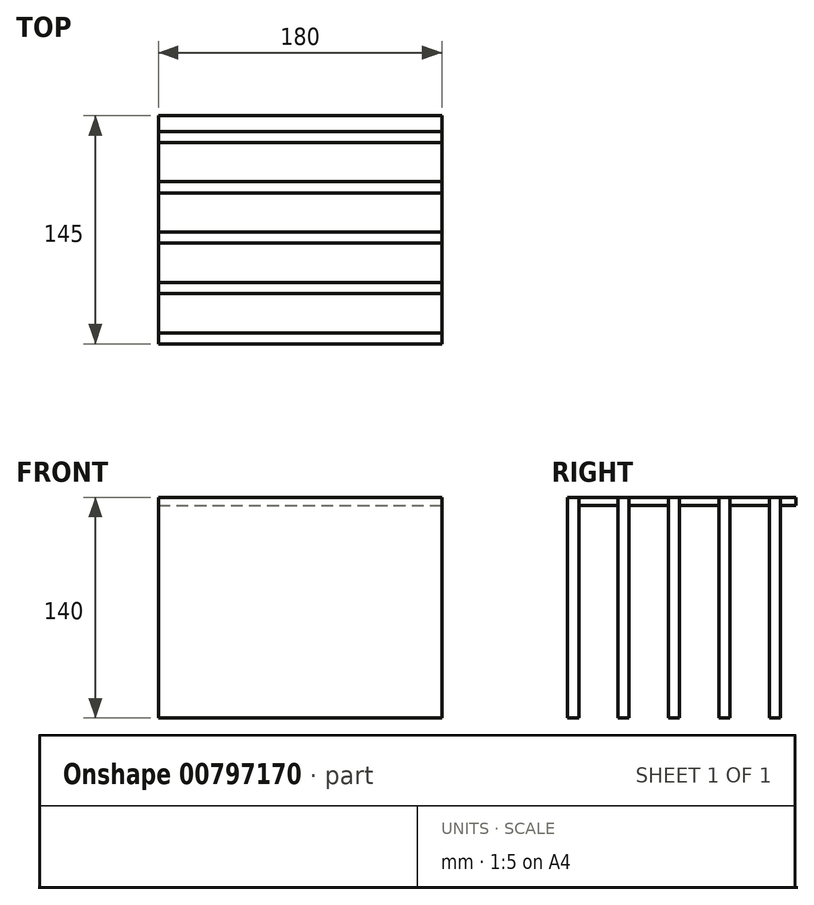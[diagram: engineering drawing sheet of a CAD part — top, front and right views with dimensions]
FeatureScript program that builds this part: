
annotation { "Feature Type Name" : "Feature", "Feature Type Description" : "" }
export const myFeature = defineFeature(function(context is Context, id is Id, definition is map)
    precondition{}
    {
        {
            var Q0;
            Q0=qCreatedBy(makeId("Top.planeOp"),FACE);
            var sketch = newSketch(context, id + "F0", { "sketchPlane" : qUnion([Q0])});
            skLineSegment(sketch, "E0.bottom", {"start": v(-72.5, 73) * mm, "end": v(107.5, 73) * mm});
            skLineSegment(sketch, "E0.top", {"start": v(-72.5, -72) * mm, "end": v(107.5, -72) * mm});
            skLineSegment(sketch, "E0.left", {"start": v(-72.5, 73) * mm, "end": v(-72.5, -72) * mm});
            skLineSegment(sketch, "E0.right", {"start": v(107.5, 73) * mm, "end": v(107.5, -72) * mm});
            skLineSegment(sketch, "E1.top", {"start": v(-72.5, -65) * mm, "end": v(107.5, -65) * mm});
            skLineSegment(sketch, "E1.left", {"start": v(-72.5, -72) * mm, "end": v(-72.5, -65) * mm});
            skLineSegment(sketch, "E1.right", {"start": v(107.5, -72) * mm, "end": v(107.5, -65) * mm});
            skLineSegment(sketch, "E2.bottom", {"start": v(-72.5, -40) * mm, "end": v(107.5, -40) * mm});
            skLineSegment(sketch, "E2.top", {"start": v(-72.5, -33) * mm, "end": v(107.5, -33) * mm});
            skLineSegment(sketch, "E2.left", {"start": v(-72.5, -40) * mm, "end": v(-72.5, -33) * mm});
            skLineSegment(sketch, "E2.right", {"start": v(107.5, -40) * mm, "end": v(107.5, -33) * mm});
            skLineSegment(sketch, "E3.bottom", {"start": v(-72.5, -8) * mm, "end": v(107.5, -8) * mm});
            skLineSegment(sketch, "E3.top", {"start": v(-72.5, -1) * mm, "end": v(107.5, -1) * mm});
            skLineSegment(sketch, "E3.left", {"start": v(-72.5, -8) * mm, "end": v(-72.5, -1) * mm});
            skLineSegment(sketch, "E3.right", {"start": v(107.5, -8) * mm, "end": v(107.5, -1) * mm});
            skLineSegment(sketch, "E4.bottom", {"start": v(-72.5, 24) * mm, "end": v(107.5, 24) * mm});
            skLineSegment(sketch, "E4.top", {"start": v(-72.5, 31) * mm, "end": v(107.5, 31) * mm});
            skLineSegment(sketch, "E4.left", {"start": v(-72.5, 24) * mm, "end": v(-72.5, 31) * mm});
            skLineSegment(sketch, "E4.right", {"start": v(107.5, 24) * mm, "end": v(107.5, 31) * mm});
            skLineSegment(sketch, "E5.bottom", {"start": v(-72.5, 56) * mm, "end": v(107.5, 56) * mm});
            skLineSegment(sketch, "E5.top", {"start": v(-72.5, 63) * mm, "end": v(107.5, 63) * mm});
            skLineSegment(sketch, "E5.left", {"start": v(-72.5, 56) * mm, "end": v(-72.5, 63) * mm});
            skLineSegment(sketch, "E5.right", {"start": v(107.5, 56) * mm, "end": v(107.5, 63) * mm});
            skSolve(sketch);
        }
        {
            var Q0;
            {var subQ0=sQuery(id+"F0.wireOp",EDGE,"E4.top");Q0=makeQuery(id+"F0.imprint","IMPRINT",FACE,{"disambiguationData":[TD([[makeQuery(id+"F0.imprint","IMPRINT",EDGE,{"derivedFrom":subQ0}),1.0]])]});}
            var Q1;
            {var subQ0=sQuery(id+"F0.wireOp",EDGE,"E0.bottom");Q1=makeQuery(id+"F0.imprint","IMPRINT",FACE,{"disambiguationData":[TD([[makeQuery(id+"F0.imprint","IMPRINT",EDGE,{"derivedFrom":subQ0}),-1.0]])]});}
            var Q2;
            {var subQ0=sQuery(id+"F0.wireOp",EDGE,"E3.top");Q2=makeQuery(id+"F0.imprint","IMPRINT",FACE,{"disambiguationData":[TD([[makeQuery(id+"F0.imprint","IMPRINT",EDGE,{"derivedFrom":subQ0}),1.0]])]});}
            var Q3;
            {var subQ0=sQuery(id+"F0.wireOp",EDGE,"E2.top");Q3=makeQuery(id+"F0.imprint","IMPRINT",FACE,{"disambiguationData":[TD([[makeQuery(id+"F0.imprint","IMPRINT",EDGE,{"derivedFrom":subQ0}),1.0]])]});}
            var Q4;
            {var subQ0=sQuery(id+"F0.wireOp",EDGE,"E1.top");Q4=makeQuery(id+"F0.imprint","IMPRINT",FACE,{"disambiguationData":[TD([[makeQuery(id+"F0.imprint","IMPRINT",EDGE,{"derivedFrom":subQ0}),1.0]])]});}
            extrude(context, id + "F1", {"entities" : qUnion([Q0, Q1, Q2, Q3, Q4]), "oppositeDirection" : true, "depth" : 5 * mm, "offsetDistance" : 25 * mm});
        }
        {
            var Q0;
            Q0=makeQuery(id+"F0.imprint","IMPRINT",FACE,{"disambiguationData":[TD([[makeQuery(id+"F0.imprint","IMPRINT",EDGE,{"derivedFrom":sQuery(id+"F0.wireOp",EDGE,"E2.bottom")}),1.0]])]});
            var Q1;
            Q1=makeQuery(id+"F0.imprint","IMPRINT",FACE,{"disambiguationData":[TD([[makeQuery(id+"F0.imprint","IMPRINT",EDGE,{"derivedFrom":sQuery(id+"F0.wireOp",EDGE,"E3.bottom")}),1.0]])]});
            var Q2;
            Q2=makeQuery(id+"F0.imprint","IMPRINT",FACE,{"disambiguationData":[TD([[makeQuery(id+"F0.imprint","IMPRINT",EDGE,{"derivedFrom":sQuery(id+"F0.wireOp",EDGE,"E4.bottom")}),1.0]])]});
            var Q3;
            Q3=makeQuery(id+"F0.imprint","IMPRINT",FACE,{"disambiguationData":[TD([[makeQuery(id+"F0.imprint","IMPRINT",EDGE,{"derivedFrom":sQuery(id+"F0.wireOp",EDGE,"E5.bottom")}),1.0]])]});
            var Q4;
            Q4=makeQuery(id+"F0.imprint","IMPRINT",FACE,{"disambiguationData":[TD([[makeQuery(id+"F0.imprint","IMPRINT",EDGE,{"derivedFrom":sQuery(id+"F0.wireOp",EDGE,"E0.top")}),1.0]])]});
            extrude(context, id + "F2", {"entities" : qUnion([Q0, Q1, Q2, Q3, Q4]), "oppositeDirection" : true, "depth" : 140 * mm, "offsetDistance" : 25 * mm});
        }
    });
